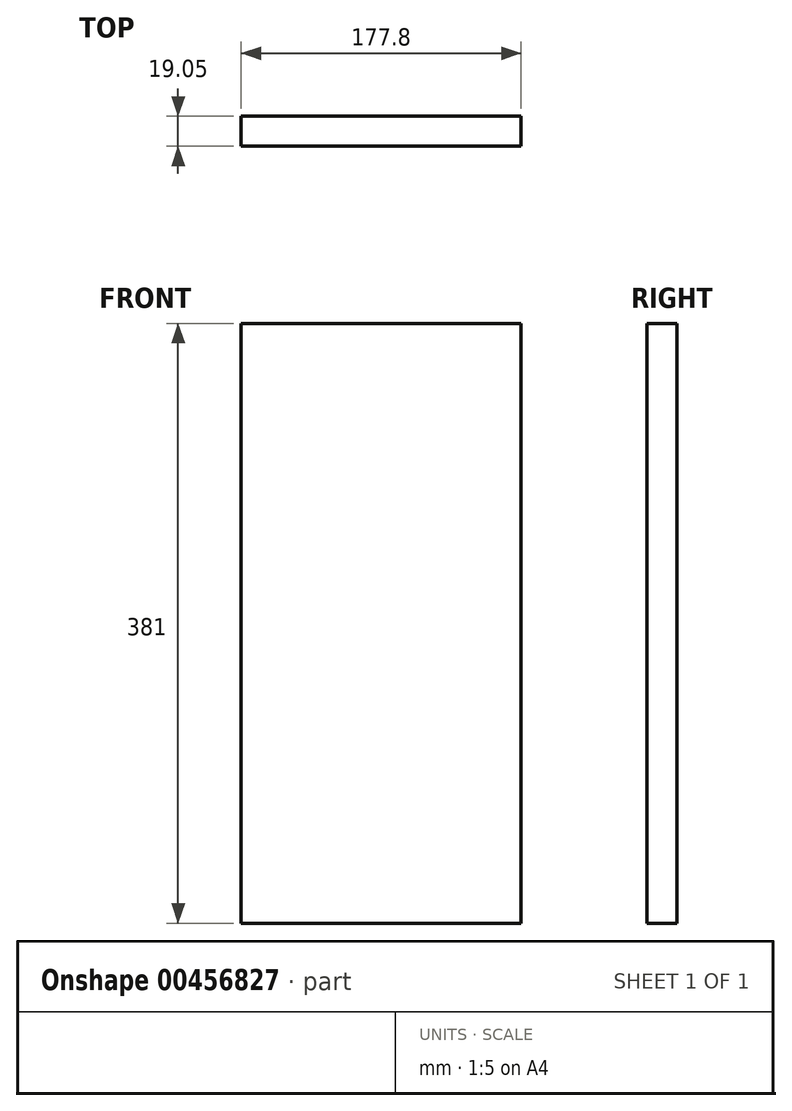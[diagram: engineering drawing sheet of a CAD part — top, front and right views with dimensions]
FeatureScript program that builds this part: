
annotation { "Feature Type Name" : "Feature", "Feature Type Description" : "" }
export const myFeature = defineFeature(function(context is Context, id is Id, definition is map)
    precondition{}
    {
        {
            var Q0;
            Q0=qCreatedBy(makeId("Front.planeOp"),FACE);
            var sketch = newSketch(context, id + "F0", { "sketchPlane" : qUnion([Q0])});
            skLineSegment(sketch, "E0", {"start": v(-87.1, 272.39) * mm, "end": v(90.7, 272.39) * mm});
            skLineSegment(sketch, "E1", {"start": v(90.7, 272.39) * mm, "end": v(90.7, -108.61) * mm});
            skLineSegment(sketch, "E2", {"start": v(90.7, -108.61) * mm, "end": v(-87.1, -108.61) * mm});
            skLineSegment(sketch, "E3", {"start": v(-87.1, -108.61) * mm, "end": v(-87.1, 272.39) * mm});
            skSolve(sketch);
        }
        {
            var Q0;
            Q0 = qSketchRegion(id + "F0", true);
            extrude(context, id + "F1", {"entities" : qUnion([Q0]), "oppositeDirection" : true, "depth" : 19.05 * mm});
        }
    });
